# Revit family: Domotics-DomesticRanges-GEWISS-CHORUS_COMMAND-PUSH-BUTTON_1M
name_source: partatom
category: Apparecchi elettrici
revit_build: Autodesk Revit 2016 (Build: 20161004_0715(x64)
units: mm (PartAtom-declared; Revit-internal decimal feet)

## family parameters
Condiviso = Sì
Host = Superficie
Mantenere orientamento annotazione = Sì
Numero OmniClass = 23.80.50.11.14
Punto di calcolo locali = Sì
Quota connettore circolare = Usa diametro
Taglio con vuoti quando caricato = Sì
Tipo di parte = Normale
Titolo OmniClass = Switches

## types (36) — shared parameters
Bidimensionale = bidimensionale pulsanti 1m : GW10153
Breaking capacity: = 1.25 In (200 position changes)
Catalogue = DOMOTICS
Catalogue Range = CHORUS - DOMESTIC RANGE
Electrocod = 0130
Glow Wire Test = 850°C
IDF = 34ea38ab-8546-4e4a-b16c-a622d8ceee5e
IDT = e30091a8-4701-4fc0-a432-b67c542ebd85
Immagine tipo = GW14153.jpg
Insulation resistance = > 5 MOhm
Larghezza pulsante = 23 mm  [stored 0.0754593 ft]
No. Chorus modules = 1
Produttore = GEWISS S.p.A.
Prolonged operation (no.of position changes) = 40.000 at In 250 V ac cosÃ˜=0,6
Prospetto di default = 1219 mm
Resistance at test voltage = 2000 V at 50 Hz for 1 minute
SEO = Push button
Simbolo_ = SIMBOLO PULSANTI : PULSANTE
Standard; = EN 60669-1
Technical sheet = https://www.gewiss.com
Terminal grip on cable traction = > 50 N
Terminal tightening capacity flexible cables (mm2) = min. 0,75 - max. 2x4
Terminal tightening capacity rigid cables (mm2) = min. 0,5 - max. 2x2,5
Thermo-pressure with ball = 125
Tipo_ = CHORUS PULSANTI 1M_BASE : GW14153 - Titanio
URL = https://www.gewiss.com
Version file RFA = 19.0
Voltage = 250 V ac
Voltage: = 250 V ac
Wiring terminals = With screw

## per-type parameters (varying)
| type | Button key | Category | Colour | Description: | Descrizione | EAN code | Modello | Number of poles | Type |
| GW14132 - Titanium - Illuminable | With diffuser | Push-button | Titanium | 1P NO - 16A illuminable | P-BUTTON 1M 1P NO 16A ILL LOC TITANIUM | 8011564265844 | GW14132 | 1P | Backlit |
| GW14133 - Titanium - Illuminable | With replaceable neutral lens | Push-button | Titanium | 1P NO - 16A illuminable | P-BUTTON 1M 1P NO 16A ILL SIG TITANIUM | 8011564265851 | GW14133 | 1P | Indicator |
| GW12139 - Black | Start | Push-button | Black | 1P NO+NC - 16 A | PUSH-BUTTON 1M 1P NO+NC 16A RUN BLACK | 8011564269583 | GW12139 | 1P | Start |
| GW10135 - White - Illuminable | With replaceable neutral lens | Push-button | White | 2P NO - 10A illuminable | PUSH-BUTTON, 1M 2P NO 16A ILL SIG WHITE | 8011564260139 | GW10135 | 2P | Indicator |
| GW10140 - White | With interlock | Double push-button | White | 1P NO+NO - 10A | P-BUTTON 1M 1P NO+NO 10A INTERLOCK WHITE | 8011564260795 | GW10140 | 1P | With interlock |
| GW14152 - Titanium | With replaceable neutral lens | Push-button | Titanium | 1P NO - 16A illuminable | P-BUTTON 1M 1P NO 16A ''KEY'' TITANIUM | 8011564277274 | GW14152 | 1P | Indicator |
| GW14134 - Titanium | Neutral | Push-button | Titanium | 2P NO - 16A | PUSH-BUTTON 1M 2P NO 16A TITANIUM | 8011564265868 | GW14134 | 2P | General |
| GW12138 - Black | Stop | Push-button | Black | 1P NC+NO - 16 A | PUSH-BUTTON 1M 1P NC+NO 16A STOP BLACK | 8011564269576 | GW12138 | 1P | Stop |
| GW12132 - Black - Illuminable | With diffuser | Push-button | Black | 1P NO - 16A illuminable | PUSH-BUTTON 1M 1P NO 16A ILL LOC BLACK | 8011564269521 | GW12132 | 1P | Backlit |
| GW12153 - Black | With replaceable neutral lens | Push-button | Black | 1P NO - 16A illuminable | PUSH-BUTTON 1M 1P NO 16A SIG.DEV. BLACK | 8011564277250 | GW12153 | 1P | Indicator |
| GW14138 - Titanium | Stop | Push-button | Titanium | 1P NC+NO - 16 A | P-BUTTON 1M 1P NC+NO 16A STOP TITANIUM | 8011564265905 | GW14138 | 1P | Stop |
| GW14151 - Titanium | With replaceable neutral lens | Push-button | Titanium | 1P NO - 16A illuminable | P-BUTTON 1M 1P NO 16A ''LIGHT'' TITANIUM | 8011564277267 | GW14151 | 1P | Indicator |
| GW12137 - Black | Neutral | Push-button | Black | 1P NC - 16A | PUSH-BUTTON 1M 1P NC 16A BLACK | 8011564269569 | GW12137 | 1P | General |
| GW12134 - Black | Neutral | Push-button | Black | 2P NO - 16A | PUSH-BUTTON 1M 2P NO 16A BLACK | 8011564269545 | GW12134 | 2P | General |
| GW10133 - White - Illuminable | With replaceable neutral lens | Push-button | White | 1P NO - 16A illuminable | PUSH-BUTTON, 1M 1P NO 16A ILL SIG WHITE | 8011564260115 | GW10133 | 1P | Indicator |
| GW12133 - Black - Illuminable | With replaceable neutral lens | Push-button | Black | 1P NO - 16A illuminable | PUSH-BUTTON 1M 1P NO 16A ILL SIG BLACK | 8011564269538 | GW12133 | 1P | Indicator |
| GW10153 - White | With replaceable neutral lens | Push-button | White | 1P NO - 16A illuminable | P-BUTTON, 1M 1P NO 16A SIG DEVICE, WHITE | 8011564277229 | GW10153 | 1P | Indicator |
| GW12140 - Black | With interlock | Double push-button | Black | 1P NO+NO - 10A | P-BUTTON 1M 1P NO+NO 10A INTERLOCK BLACK | 8011564269590 | GW12140 | 1P | With interlock |
| GW12131 - Black | Neutral | Push-button | Black | 1P NO - 16A | PUSH-BUTTON 1M 1P NO 16A BLACK | 8011564267190 | GW12131 | 1P | General |
| GW12135 - Black - Illuminable | With replaceable neutral lens | Push-button | Black | 2P NO - 10A illuminable | PUSH-BUTTON 1M 2P NO 16A ILL SIG BLACK | 8011564269552 | GW12135 | 2P | Indicator |
| GW14131 - Titanium | Neutral | Push-button | Titanium | 1P NO - 16A | PUSH-BUTTON 1M 1P NO 16A TITANIUM | 8011564265837 | GW14131 | 1P | General |
| GW10139 - White | Start | Push-button | White | 1P NO+NC - 16 A | PUSH-BUTTON, 1M 1P NO+NC 16A RUN WHITE | 8011564260788 | GW10139 | 1P | Start |
| GW14139 - Titanium | Start | Push-button | Titanium | 1P NO+NC - 16 A | P-BUTTON 1M 1P NO+NC 16A RUN TITANIUM | 8011564265912 | GW14139 | 1P | Start |
| GW10134 - White | Neutral | Push-button | White | 2P NO - 16A | PUSH-BUTTON, 1M 2P NO 16A WHITE | 8011564260122 | GW10134 | 2P | General |
| GW14137 - Titanium | Neutral | Push-button | Titanium | 1P NC - 16A | PUSH-BUTTON 1M 1P NC 16A TITANIUM | 8011564265899 | GW14137 | 1P | General |
| GW10131 - White | Neutral | Push-button | White | 1P NO - 16A | PUSH-BUTTON, 1M 1P NO 16A WHITE | 8011564257849 | GW10131 | 1P | General |
| GW10138 - White | Stop | Push-button | White | 1P NC+NO - 16 A | PUSH-BUTTON, 1M 1P NC+NO 16A STOP WHITE | 8011564260771 | GW10138 | 1P | Stop |
| GW10132 - White - Illuminable | With diffuser | Push-button | White | 1P NO - 16A illuminable | PUSH-BUTTON, 1M 1P NO 16A ILL LOC WHITE | 8011564260108 | GW10132 | 1P | Backlit |
| GW10137 - White | Neutral | Push-button | White | 1P NC - 16A | PUSH-BUTTON, 1M 1P NC 16A WHITE | 8011564260146 | GW10137 | 1P | General |
| GW10151 - White | With replaceable neutral lens | Push-button | White | 1P NO - 16A illuminable | P-BUTTON, 1M 1P NO 16A ''LIGHT''  WHITE | 8011564277007 | GW10151 | 1P | Indicator |
| GW12152 - Black | With replaceable neutral lens | Push-button | Black | 1P NO - 16A illuminable | P-BUTTON 1M 1P NO 16A 'KEY' BLACK | 8011564277243 | GW12152 | 1P | Indicator |
| GW14140 - Titanium | With interlock | Double push-button | Titanium | 1P NO+NO - 10A | P-BUTTON 1M 1P NO+NO 10A INTERLOCK T | 8011564265929 | GW14140 | 1P | With interlock |
| GW14153 - Titanium | With replaceable neutral lens | Push-button | Titanium | 1P NO - 16A illuminable | P-BUTTON 1M 1P NO 16A SIG DEV. TITANIUM | 8011564277281 | GW14153 | 1P | Indicator |
| GW10152 - White | With replaceable neutral lens | Push-button | White | 1P NO - 16A illuminable | P-BUTTON, 1M 1P NO 16A 'KEY', WHITE | 8011564277212 | GW10152 | 1P | Indicator |
| GW14135 - Titanium - Illuminable | With replaceable neutral lens | Push-button | Titanium | 2P NO - 10A illuminable | P-BUTTON 1M 2P NO 16A ILL SIG TITANIUM | 8011564265875 | GW14135 | 2P | Indicator |
| GW12151 - Black | With replaceable neutral lens | Push-button | Black | 1P NO - 16A illuminable | P-BUTTON 1M 1P NO 16A 'LIGHT' BLACK | 8011564277236 | GW12151 | 1P | Indicator |

note: source unit labels omitted for Thermo-pressure with ball — the stored unit's dimension contradicts the parameter name (converter mislabeling)

note: [stored X ft] marks values corroborated as IEEE doubles in the binary element streams (Revit-internal decimal feet)

## geometry (parser evidence)
native form markers: Sweep x1
no freeform markers — native parametric forms only
